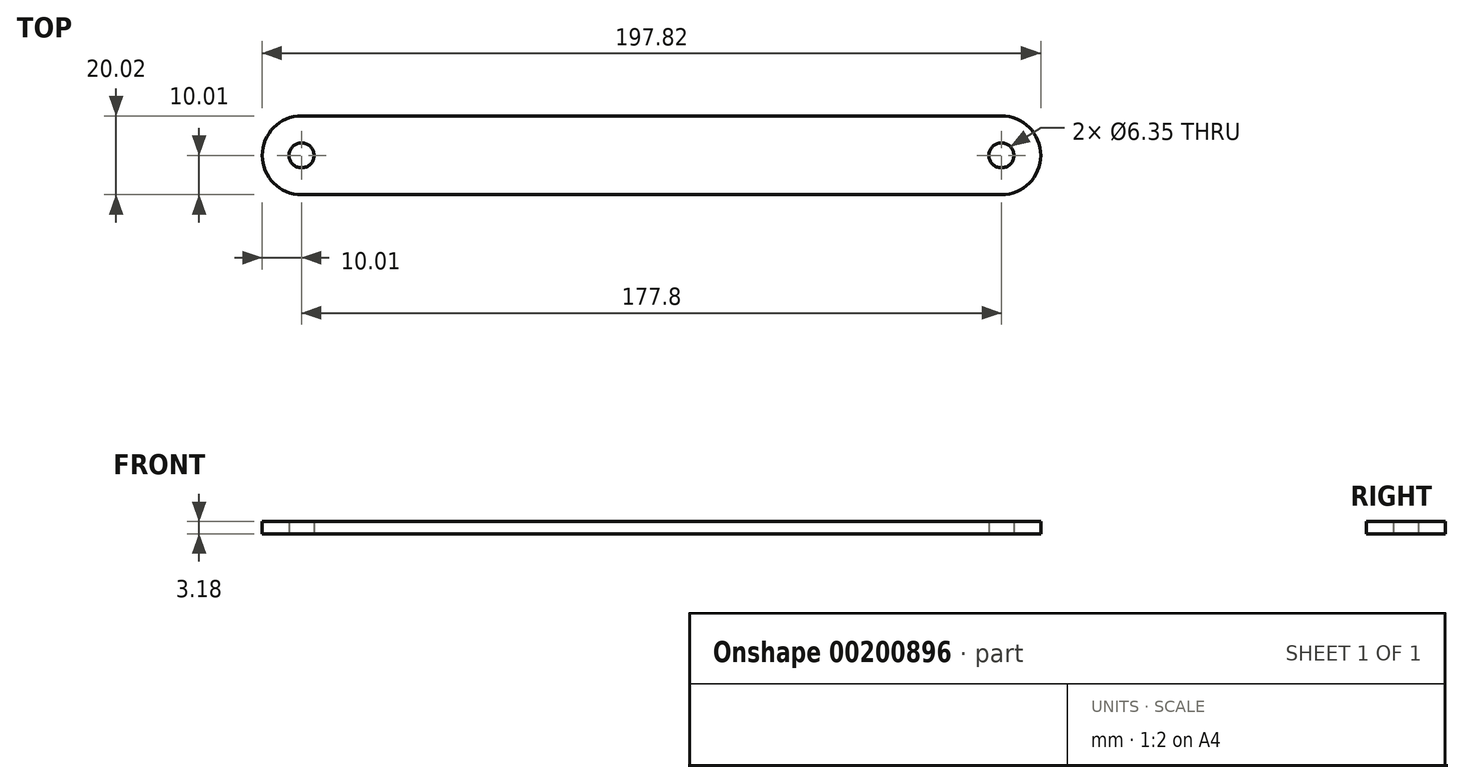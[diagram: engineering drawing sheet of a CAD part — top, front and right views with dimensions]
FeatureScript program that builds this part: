
annotation { "Feature Type Name" : "Feature", "Feature Type Description" : "" }
export const myFeature = defineFeature(function(context is Context, id is Id, definition is map)
    precondition{}
    {
        {
            var Q0;
            Q0=qCreatedBy(makeId("Top.planeOp"),FACE);
            var sketch = newSketch(context, id + "F0", { "sketchPlane" : qUnion([Q0])});
            skLineSegment(sketch, "E0.bottom", {"start": v(-88.9, 10) * mm, "end": v(88.9, 10) * mm});
            skLineSegment(sketch, "E0.top", {"start": v(-88.9, -10) * mm, "end": v(88.9, -10) * mm});
            skCircle(sketch, "E1", {"center": v(-88.9, 0) * mm, "radius": 3.18 * mm});
            skCircle(sketch, "E2", {"center": v(88.9, 0) * mm, "radius": 3.18 * mm});
            skArc(sketch, "E3", {"start": v(-88.9, 10) * mm, "mid": v(-98.9, 0) * mm, "end": v(-88.9, -10) * mm});
            skArc(sketch, "E4", {"start": v(88.9, -10) * mm, "mid": v(98.9, 0) * mm, "end": v(88.9, 10) * mm});
            skSolve(sketch);
        }
        {
            var Q0;
            Q0=makeQuery(id+"F0.imprint","IMPRINT",FACE,{"disambiguationData":[TD([[makeQuery(id+"F0.imprint","IMPRINT",EDGE,{"derivedFrom":sQuery(id+"F0.wireOp",EDGE,"E0.bottom")}),-1.0]])]});
            extrude(context, id + "F1", {"entities" : qUnion([Q0]), "depth" : 3.17 * mm});
        }
    });
